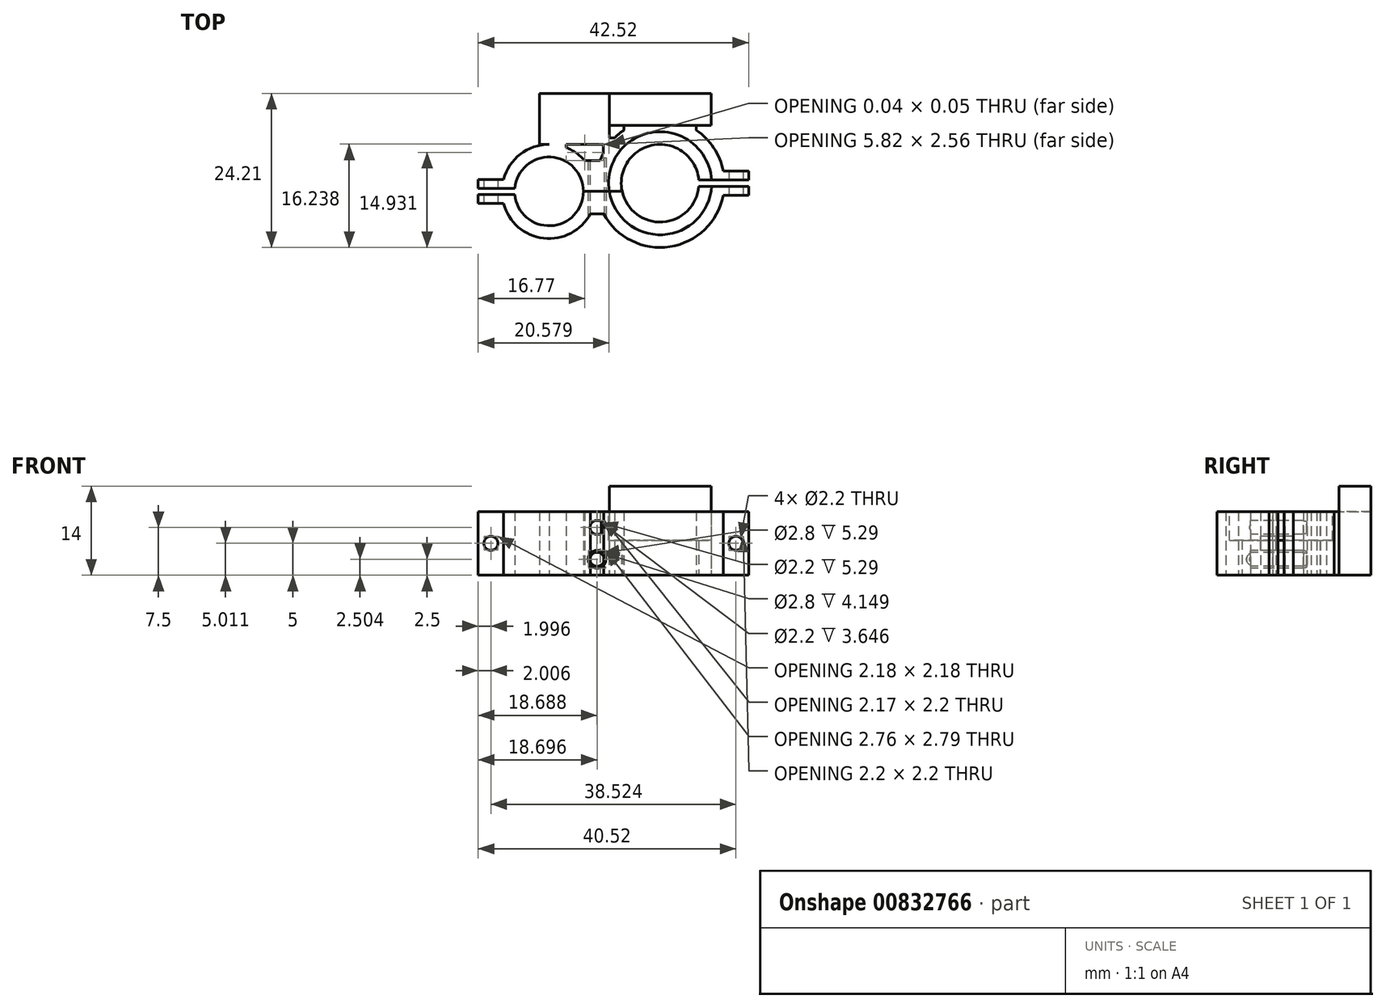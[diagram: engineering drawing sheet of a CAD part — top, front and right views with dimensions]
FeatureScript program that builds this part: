
annotation { "Feature Type Name" : "Feature", "Feature Type Description" : "" }
export const myFeature = defineFeature(function(context is Context, id is Id, definition is map)
    precondition{}
    {
        {
            var Q0;
            Q0=qCreatedBy(makeId("Top.planeOp"),FACE);
            var sketch = newSketch(context, id + "F0", { "sketchPlane" : qUnion([Q0])});
            skArc(sketch, "E0", {"start": v(6.08, 0.5) * mm, "mid": v(-6.1, 0) * mm, "end": v(6.08, -0.5) * mm});
            skArc(sketch, "E1", {"start": v(9.92, 1.9) * mm, "mid": v(8.44, 5.55) * mm, "end": v(5.68, 8.35) * mm});
            skLineSegment(sketch, "E2", {"start": v(0, 15.92) * mm, "end": v(0, -15.65) * mm, "construction": true});
            skLineSegment(sketch, "E3", {"start": v(0, 9.11) * mm, "end": v(8, 9.11) * mm});
            skLineSegment(sketch, "E4", {"start": v(8, 9.11) * mm, "end": v(8, 14.11) * mm});
            skLineSegment(sketch, "E5", {"start": v(8, 14.11) * mm, "end": v(0, 14.11) * mm});
            skLineSegment(sketch, "E6.MirrorCS", {"start": v(0, 9.11) * mm, "end": v(-8, 9.11) * mm});
            skLineSegment(sketch, "E7.MirrorCS", {"start": v(-8, 9.11) * mm, "end": v(-8, 14.11) * mm});
            skLineSegment(sketch, "E8.MirrorCS", {"start": v(-8, 14.11) * mm, "end": v(0, 14.11) * mm});
            skLineSegment(sketch, "E9", {"start": v(-18.97, 14.11) * mm, "end": v(-8, 14.11) * mm});
            skLineSegment(sketch, "E10", {"start": v(-8, 9.11) * mm, "end": v(-8, 7.12) * mm});
            skLineSegment(sketch, "E11", {"start": v(-8, 6.11) * mm, "end": v(-8.04, 6.11) * mm});
            skLineSegment(sketch, "E12", {"start": v(-18.97, 6.11) * mm, "end": v(-18.97, 14.11) * mm});
            skArc(sketch, "E13", {"start": v(-24.6, -3.19) * mm, "mid": v(-18.31, -8.64) * mm, "end": v(-10.93, -4.79) * mm});
            skArc(sketch, "E14", {"start": v(-22.83, -1.79) * mm, "mid": v(-12.05, -1.29) * mm, "end": v(-22.83, -0.79) * mm});
            skLineSegment(sketch, "E15", {"start": v(0, 0) * mm, "end": v(15.85, 0) * mm, "construction": true});
            skLineSegment(sketch, "E16", {"start": v(6.08, 0.5) * mm, "end": v(13.92, 0.5) * mm});
            skLineSegment(sketch, "E17", {"start": v(13.92, 0.5) * mm, "end": v(13.92, 1.9) * mm});
            skLineSegment(sketch, "E18", {"start": v(13.92, 1.9) * mm, "end": v(9.92, 1.9) * mm});
            skLineSegment(sketch, "E19.MirrorCS", {"start": v(6.08, -0.5) * mm, "end": v(13.92, -0.5) * mm});
            skLineSegment(sketch, "E20.MirrorCS", {"start": v(13.92, -1.9) * mm, "end": v(9.92, -1.9) * mm});
            skLineSegment(sketch, "E21.MirrorCS", {"start": v(0, -15.92) * mm, "end": v(0, 15.65) * mm, "construction": true});
            skLineSegment(sketch, "E22.MirrorCS", {"start": v(13.92, -0.5) * mm, "end": v(13.92, -1.9) * mm});
            skLineSegment(sketch, "E23", {"start": v(-17.45, -1.29) * mm, "end": v(-26.78, -1.29) * mm, "construction": true});
            skLineSegment(sketch, "E24", {"start": v(-22.83, -0.79) * mm, "end": v(-28.6, -0.79) * mm});
            skLineSegment(sketch, "E25", {"start": v(-28.6, -0.79) * mm, "end": v(-28.6, 0.61) * mm});
            skLineSegment(sketch, "E26", {"start": v(-28.6, 0.61) * mm, "end": v(-24.6, 0.61) * mm});
            skLineSegment(sketch, "E27.MirrorCS", {"start": v(-22.83, -1.79) * mm, "end": v(-28.6, -1.79) * mm});
            skLineSegment(sketch, "E28.MirrorCS", {"start": v(-28.6, -1.79) * mm, "end": v(-28.6, -3.19) * mm});
            skLineSegment(sketch, "E29.MirrorCS", {"start": v(-28.6, -3.19) * mm, "end": v(-24.6, -3.19) * mm});
            skLineSegment(sketch, "E30", {"start": v(-11.86, 3.55) * mm, "end": v(-9.45, 3.55) * mm});
            skLineSegment(sketch, "E31", {"start": v(-10.93, -4.79) * mm, "end": v(-8.9, -4.79) * mm});
            skArc(sketch, "E32.trimOffspring", {"start": v(-8.9, -4.79) * mm, "mid": v(1.53, -9.98) * mm, "end": v(9.92, -1.9) * mm});
            skArc(sketch, "E33.trimOffspring", {"start": v(-11.86, 3.55) * mm, "mid": v(-13.17, 4.75) * mm, "end": v(-14.74, 5.6) * mm});
            skLineSegment(sketch, "E34", {"start": v(-8.92, 6.11) * mm, "end": v(-8.92, 4.74) * mm});
            skLineSegment(sketch, "E35", {"start": v(-8, 7.12) * mm, "end": v(-7.17, 7.12) * mm});
            skLineSegment(sketch, "E36", {"start": v(-14.74, 6.11) * mm, "end": v(-14.74, 5.6) * mm});
            skLineSegment(sketch, "E37", {"start": v(5.68, 9.11) * mm, "end": v(5.68, 8.35) * mm});
            skLineSegment(sketch, "E38.trimOffspring", {"start": v(-17.45, 6.11) * mm, "end": v(-18.97, 6.11) * mm});
            skArc(sketch, "E39.trimOffspring", {"start": v(-17.45, 6.11) * mm, "mid": v(-21.96, 4.58) * mm, "end": v(-24.6, 0.61) * mm});
            skLineSegment(sketch, "E40.trimOffspring", {"start": v(-8.92, 6.11) * mm, "end": v(-14.74, 6.11) * mm});
            skArc(sketch, "E41.trimOffspring", {"start": v(-8.92, 4.74) * mm, "mid": v(-9.2, 4.15) * mm, "end": v(-9.45, 3.55) * mm});
            skLineSegment(sketch, "E42.trimOffspring", {"start": v(-8, 6.17) * mm, "end": v(-8, 6.11) * mm});
            skArc(sketch, "E43.trimOffspring", {"start": v(-8, 6.17) * mm, "mid": v(-8.02, 6.14) * mm, "end": v(-8.04, 6.11) * mm});
            skArc(sketch, "E44.trimOffspring", {"start": v(-5.68, 8.35) * mm, "mid": v(-6.45, 7.77) * mm, "end": v(-7.17, 7.12) * mm});
            skLineSegment(sketch, "E45", {"start": v(-12.05, -1.29) * mm, "end": v(-5.96, -1.29) * mm});
            skLineSegment(sketch, "E46.MirrorCS", {"start": v(-5.68, 9.11) * mm, "end": v(-5.68, 8.35) * mm});
            skSolve(sketch);
        }
        {
            var Q0;
            Q0=makeQuery(id+"F0.imprint","IMPRINT",FACE,{"disambiguationData":[TD([[makeQuery(id+"F0.imprint","IMPRINT",EDGE,{"derivedFrom":sQuery(id+"F0.wireOp",EDGE,"E0")}),-1.0]])]});
            extrude(context, id + "F1", {"entities" : qUnion([Q0]), "depth" : 10 * mm, "offsetDistance" : 25 * mm});
        }
        {
            var Q0;
            Q0=makeQuery(id+"F0.imprint","IMPRINT",FACE,{"disambiguationData":[TD([[makeQuery(id+"F0.imprint","IMPRINT",EDGE,{"derivedFrom":sQuery(id+"F0.wireOp",EDGE,"E1")}),1.0]])]});
            extrude(context, id + "F2", {"entities" : qUnion([Q0]), "depth" : 10 * mm, "offsetDistance" : 25 * mm});
        }
        {
            var Q0;
            {var subQ0=sQuery(id+"F0.wireOp",EDGE,"E4");Q0=makeQuery(id+"F0.imprint","IMPRINT",FACE,{"disambiguationData":[TD([[makeQuery(id+"F0.imprint","IMPRINT",EDGE,{"derivedFrom":subQ0}),1.0]])]});}
            extrude(context, id + "F3", {"entities" : qUnion([Q0]), "operationType" : NewBodyOperationType.ADD, "depth" : 14 * mm, "offsetDistance" : 25 * mm});
        }
        {
            var Q0;
            Q0=makeQuery(id+"F1.opExtrude","CAP_FACE",FACE,{"disambiguationData":[OSD([sQuery(id+"F0.wireOp",EDGE,"E0"),sQuery(id+"F0.wireOp",EDGE,"E1"),sQuery(id+"F0.wireOp",EDGE,"E3"),sQuery(id+"F0.wireOp",EDGE,"E6.MirrorCS"),sQuery(id+"F0.wireOp",EDGE,"E7.MirrorCS"),sQuery(id+"F0.wireOp",EDGE,"E9"),sQuery(id+"F0.wireOp",EDGE,"E10"),sQuery(id+"F0.wireOp",EDGE,"E11"),sQuery(id+"F0.wireOp",EDGE,"E12"),sQuery(id+"F0.wireOp",EDGE,"E13"),sQuery(id+"F0.wireOp",EDGE,"E14"),sQuery(id+"F0.wireOp",EDGE,"E16"),sQuery(id+"F0.wireOp",EDGE,"E17"),sQuery(id+"F0.wireOp",EDGE,"E18"),sQuery(id+"F0.wireOp",EDGE,"E19.MirrorCS"),sQuery(id+"F0.wireOp",EDGE,"E20.MirrorCS"),sQuery(id+"F0.wireOp",EDGE,"E22.MirrorCS"),sQuery(id+"F0.wireOp",EDGE,"E24"),sQuery(id+"F0.wireOp",EDGE,"E25"),sQuery(id+"F0.wireOp",EDGE,"E26"),sQuery(id+"F0.wireOp",EDGE,"E27.MirrorCS"),sQuery(id+"F0.wireOp",EDGE,"E28.MirrorCS"),sQuery(id+"F0.wireOp",EDGE,"E29.MirrorCS"),sQuery(id+"F0.wireOp",EDGE,"E30"),sQuery(id+"F0.wireOp",EDGE,"E31"),sQuery(id+"F0.wireOp",EDGE,"E32.trimOffspring"),sQuery(id+"F0.wireOp",EDGE,"E33.trimOffspring"),sQuery(id+"F0.wireOp",EDGE,"E34"),sQuery(id+"F0.wireOp",EDGE,"E35"),sQuery(id+"F0.wireOp",EDGE,"E36"),sQuery(id+"F0.wireOp",EDGE,"E37"),sQuery(id+"F0.wireOp",EDGE,"E38.trimOffspring"),sQuery(id+"F0.wireOp",EDGE,"E39.trimOffspring"),sQuery(id+"F0.wireOp",EDGE,"E40.trimOffspring"),sQuery(id+"F0.wireOp",EDGE,"E41.trimOffspring"),sQuery(id+"F0.wireOp",EDGE,"E42.trimOffspring"),sQuery(id+"F0.wireOp",EDGE,"E43.trimOffspring"),sQuery(id+"F0.wireOp",EDGE,"E44.trimOffspring")])],"isStart":false});
            var sketch = newSketch(context, id + "F4", { "sketchPlane" : qUnion([Q0])});
            skCircle(sketch, "E47", {"center": v(0, 0) * mm, "radius": 8.1 * mm});
            skSolve(sketch);
        }
        {
            var Q0;
            {var subQ5=makeQuery(id+"F1.opExtrude","CAP_EDGE",EDGE,{"disambiguationData":[OSD([sQuery(id+"F0.wireOp",EDGE,"E0")])],"isStart":false});Q0=makeQuery(id+"F4.imprint","IMPRINT",FACE,{"disambiguationData":[TD([[makeQuery(id+"F4.imprint","IMPRINT",EDGE,{"derivedFrom":subQ5}),-1.0]])]});}
            extrude(context, id + "F5", {"entities" : qUnion([Q0]), "operationType" : NewBodyOperationType.REMOVE, "oppositeDirection" : true, "depth" : 4.5 * mm, "offsetDistance" : 25 * mm});
        }
        {
            var Q0;
            {var subQ5=makeQuery(id+"F1.opExtrude","CAP_EDGE",EDGE,{"disambiguationData":[OSD([sQuery(id+"F0.wireOp",EDGE,"E0")])],"isStart":false});Q0=makeQuery(id+"F4.imprint","IMPRINT",FACE,{"disambiguationData":[TD([[makeQuery(id+"F4.imprint","IMPRINT",EDGE,{"derivedFrom":subQ5}),1.0]])]});}
            extrude(context, id + "F6", {"entities" : qUnion([Q0]), "operationType" : NewBodyOperationType.REMOVE, "oppositeDirection" : true, "depth" : 4.5 * mm, "offsetDistance" : 25 * mm});
        }
        {
            var Q0;
            Q0=qCreatedBy(makeId("Front.planeOp"),FACE);
            cPlane(context, id + "F7", {"entities" : qUnion([Q0]), "cplaneType" : CPlaneType.OFFSET, "offset" : 10 * mm, "width" : 150 * mm, "height" : 150 * mm});
        }
        {
            var Q0;
            Q0=qCreatedBy(id+"F7.planeOp",FACE);
            var sketch = newSketch(context, id + "F8", { "sketchPlane" : qUnion([Q0])});
            skPoint(sketch, "E48.0", {"position": v(-8.9, 5) * mm});
            skLineSegment(sketch, "E49", {"start": v(-30.15, 5) * mm, "end": v(15.27, 5) * mm, "construction": true});
            skPoint(sketch, "E50.0", {"position": v(-9.91, 10) * mm});
            skCircle(sketch, "E51", {"center": v(-9.91, 7.5) * mm, "radius": 1.1 * mm});
            skCircle(sketch, "E52.MirrorC", {"center": v(-9.91, 2.5) * mm, "radius": 1.1 * mm});
            skCircle(sketch, "E53", {"center": v(-9.91, 7.5) * mm, "radius": 1.4 * mm});
            skCircle(sketch, "E54", {"center": v(-9.91, 7.5) * mm, "radius": 2.85 * mm});
            skCircle(sketch, "E55.MirrorC", {"center": v(-9.91, 2.5) * mm, "radius": 1.4 * mm});
            skCircle(sketch, "E56.MirrorC", {"center": v(-9.91, 2.5) * mm, "radius": 2.85 * mm});
            skLineSegment(sketch, "E57.0.0", {"start": v(-28.6, 0) * mm, "end": v(-24.6, 0) * mm});
            skLineSegment(sketch, "E57.0.1", {"start": v(-24.6, 0) * mm, "end": v(-24.6, 10) * mm});
            skLineSegment(sketch, "E57.0.2", {"start": v(-24.6, 10) * mm, "end": v(-28.6, 10) * mm});
            skLineSegment(sketch, "E57.0.3", {"start": v(-28.6, 10) * mm, "end": v(-28.6, 0) * mm});
            skLineSegment(sketch, "E58.0.0", {"start": v(9.92, 0) * mm, "end": v(13.92, 0) * mm});
            skLineSegment(sketch, "E58.0.1", {"start": v(13.92, 0) * mm, "end": v(13.92, 10) * mm});
            skLineSegment(sketch, "E58.0.2", {"start": v(13.92, 10) * mm, "end": v(9.92, 10) * mm});
            skLineSegment(sketch, "E58.0.3", {"start": v(9.92, 10) * mm, "end": v(9.92, 0) * mm});
            skCircle(sketch, "E59", {"center": v(-26.6, 5) * mm, "radius": 1.1 * mm});
            skPoint(sketch, "E59.centerSnap0", {"position": v(-26.6, 10) * mm});
            skCircle(sketch, "E60", {"center": v(-26.6, 5) * mm, "radius": 1.4 * mm});
            skCircle(sketch, "E61", {"center": v(11.92, 5) * mm, "radius": 1.1 * mm});
            skPoint(sketch, "E61.centerSnap0", {"position": v(11.92, 10) * mm});
            skCircle(sketch, "E62", {"center": v(11.92, 5) * mm, "radius": 1.4 * mm});
            skPoint(sketch, "E63.0", {"position": v(0, 14) * mm});
            skLineSegment(sketch, "E64", {"start": v(0, 14) * mm, "end": v(0, 10.02) * mm, "construction": true});
            skCircle(sketch, "E65", {"center": v(-6.04, 12.3) * mm, "radius": 1.4 * mm});
            skSolve(sketch);
        }
        {
            var Q0;
            Q0=makeQuery(id+"F8.imprint","IMPRINT",FACE,{"disambiguationData":[TD([[makeQuery(id+"F8.imprint","IMPRINT",EDGE,{"derivedFrom":sQuery(id+"F8.wireOp",EDGE,"E59")}),1.0]])]});
            var Q1;
            Q1=makeQuery(id+"F8.imprint","IMPRINT",FACE,{"disambiguationData":[TD([[makeQuery(id+"F8.imprint","IMPRINT",EDGE,{"derivedFrom":sQuery(id+"F8.wireOp",EDGE,"E51")}),1.0]])]});
            var Q2;
            Q2=makeQuery(id+"F8.imprint","IMPRINT",FACE,{"disambiguationData":[TD([[makeQuery(id+"F8.imprint","IMPRINT",EDGE,{"derivedFrom":sQuery(id+"F8.wireOp",EDGE,"E52.MirrorC")}),-1.0]])]});
            var Q3;
            Q3=makeQuery(id+"F8.imprint","IMPRINT",FACE,{"disambiguationData":[TD([[makeQuery(id+"F8.imprint","IMPRINT",EDGE,{"derivedFrom":sQuery(id+"F8.wireOp",EDGE,"E61")}),1.0]])]});
            extrude(context, id + "F9", {"entities" : qUnion([Q0, Q1, Q2, Q3]), "operationType" : NewBodyOperationType.REMOVE, "oppositeDirection" : true, "depth" : 14 * mm, "offsetDistance" : 25 * mm});
        }
    });
